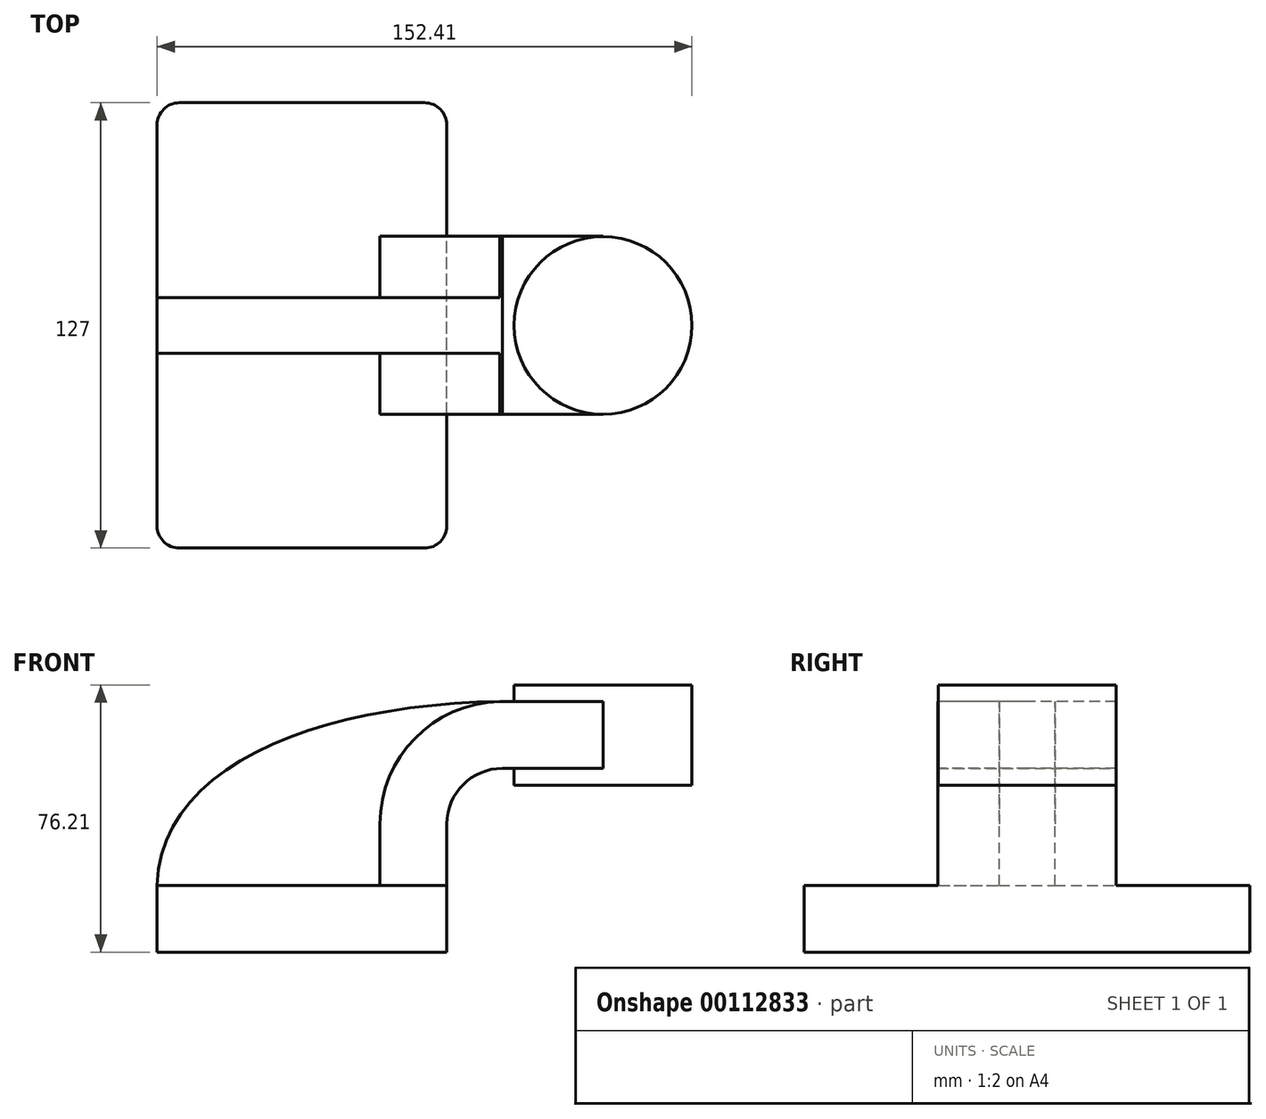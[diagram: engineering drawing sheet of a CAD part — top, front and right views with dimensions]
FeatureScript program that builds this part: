
annotation { "Feature Type Name" : "Feature", "Feature Type Description" : "" }
export const myFeature = defineFeature(function(context is Context, id is Id, definition is map)
    precondition{}
    {
        {
            var Q0;
            Q0=qCreatedBy(makeId("Front.planeOp"),FACE);
            var sketch = newSketch(context, id + "F0", { "sketchPlane" : qUnion([Q0])});
            skLineSegment(sketch, "E0.bottom", {"start": v(41.27, 9.53) * mm, "end": v(-41.28, 9.53) * mm});
            skLineSegment(sketch, "E0.top", {"start": v(41.28, -9.52) * mm, "end": v(-41.27, -9.52) * mm});
            skLineSegment(sketch, "E0.left", {"start": v(41.27, 9.53) * mm, "end": v(41.28, -9.52) * mm});
            skLineSegment(sketch, "E0.right", {"start": v(-41.28, 9.53) * mm, "end": v(-41.27, -9.52) * mm});
            skPoint(sketch, "E0.middle", {"position": v(0, 0) * mm});
            skLineSegment(sketch, "E1.bottom", {"start": v(111.12, 38.1) * mm, "end": v(60.32, 38.1) * mm});
            skLineSegment(sketch, "E1.top", {"start": v(111.12, 66.68) * mm, "end": v(60.32, 66.68) * mm});
            skLineSegment(sketch, "E1.left", {"start": v(111.12, 38.1) * mm, "end": v(111.12, 66.68) * mm});
            skLineSegment(sketch, "E1.right", {"start": v(60.32, 38.1) * mm, "end": v(60.32, 66.68) * mm});
            skPoint(sketch, "E1.middle", {"position": v(85.72, 52.39) * mm});
            skLineSegment(sketch, "E2", {"start": v(41.27, 9.53) * mm, "end": v(41.27, 27) * mm});
            skArc(sketch, "E3", {"start": v(41.27, 27) * mm, "mid": v(45.92, 38.23) * mm, "end": v(57.15, 42.88) * mm});
            skLineSegment(sketch, "E4", {"start": v(57.15, 42.88) * mm, "end": v(85.79, 42.88) * mm});
            skLineSegment(sketch, "E5.0", {"start": v(57.15, 61.93) * mm, "end": v(85.79, 61.93) * mm});
            skArc(sketch, "E5.1", {"start": v(22.22, 27) * mm, "mid": v(32.45, 51.7) * mm, "end": v(57.15, 61.93) * mm});
            skLineSegment(sketch, "E5.2", {"start": v(22.22, 9.53) * mm, "end": v(22.22, 27) * mm});
            skLineSegment(sketch, "E6", {"start": v(85.79, 38.1) * mm, "end": v(85.79, 66.68) * mm});
            skPoint(sketch, "E6.startSnap0", {"position": v(85.72, 38.1) * mm});
            skFitSpline(sketch, "E7", {"points": [v(-41.28, 9.52) * mm, v(57.15, 61.93) * mm], "startDerivative": vector(3.01, 105.74) * mm, "endDerivative": vector(150.34, 1.5) * mm});
            skSolve(sketch);
        }
        {
            var Q0;
            Q0=makeQuery(id+"F0.imprint","IMPRINT",FACE,{"disambiguationData":[TD([[makeQuery(id+"F0.imprint","IMPRINT",EDGE,{"derivedFrom":sQuery(id+"F0.wireOp",EDGE,"E0.top")}),-1.0]])]});
            extrude(context, id + "F1", {"entities" : qUnion([Q0]), "endBound" : BoundingType.SYMMETRIC, "depth" : 127 * mm});
        }
        {
            var Q0;
            {var subQ1=sQuery(id+"F0.wireOp",EDGE,"E2");Q0=makeQuery(id+"F0.imprint","IMPRINT",FACE,{"disambiguationData":[TD([[makeQuery(id+"F0.imprint","IMPRINT",EDGE,{"derivedFrom":subQ1}),1.0]])]});}
            var Q1;
            {var subQ0=sQuery(id+"F0.wireOp",EDGE,"E4");var subQ1=sQuery(id+"F0.wireOp",EDGE,"E1.right");var subQ2=makeQuery(id+"F0.imprint","INTERSECT",VERTEX,{"derivedFrom":[subQ1,subQ0]});Q1=makeQuery(id+"F0.imprint","IMPRINT",FACE,{"disambiguationData":[TD([[makeQuery(id+"F0.imprint","IMPRINT",EDGE,{"disambiguationData":[TD([[subQ2,-1.0]])],"derivedFrom":subQ1}),-1.0]])]});}
            extrude(context, id + "F2", {"entities" : qUnion([Q0, Q1]), "operationType" : NewBodyOperationType.ADD, "endBound" : BoundingType.SYMMETRIC, "depth" : 50.8 * mm});
        }
        {
            var Q0;
            {var subQ3=sQuery(id+"F0.wireOp",EDGE,"E5.2");Q0=makeQuery(id+"F0.imprint","IMPRINT",FACE,{"disambiguationData":[TD([[makeQuery(id+"F0.imprint","IMPRINT",EDGE,{"derivedFrom":subQ3}),1.0]])]});}
            extrude(context, id + "F3", {"entities" : qUnion([Q0]), "operationType" : NewBodyOperationType.ADD, "endBound" : BoundingType.SYMMETRIC, "depth" : 15.88 * mm});
        }
        {
            var Q0;
            {var subQ0=sQuery(id+"F0.wireOp",EDGE,"E1.left");Q0=makeQuery(id+"F0.imprint","IMPRINT",FACE,{"disambiguationData":[TD([[makeQuery(id+"F0.imprint","IMPRINT",EDGE,{"derivedFrom":subQ0}),1.0]])]});}
            var Q1;
            Q1=sQuery(id+"F0.wireOp",EDGE,"E6");
            revolve(context, id + "F4", {"operationType" : NewBodyOperationType.ADD, "entities" : qUnion([Q0]), "axis" : qUnion([Q1]), "revolveType" : RevolveType.FULL});
        }
        {
            var Q0;
            Q0=makeQuery(id+"F1.opExtrude","CAP_EDGE",EDGE,{"disambiguationData":[OSD([sQuery(id+"F0.wireOp",EDGE,"E0.left")])],"isStart":false});
            var Q1;
            Q1=makeQuery(id+"F1.opExtrude","CAP_EDGE",EDGE,{"disambiguationData":[OSD([sQuery(id+"F0.wireOp",EDGE,"E0.right")])],"isStart":false});
            var Q2;
            Q2=makeQuery(id+"F1.opExtrude","CAP_EDGE",EDGE,{"disambiguationData":[OSD([sQuery(id+"F0.wireOp",EDGE,"E0.left")])],"isStart":true});
            var Q3;
            Q3=makeQuery(id+"F1.opExtrude","CAP_EDGE",EDGE,{"disambiguationData":[OSD([sQuery(id+"F0.wireOp",EDGE,"E0.right")])],"isStart":true});
            fillet(context, id + "F5", {"entities" : qUnion([Q0, Q1, Q2, Q3]), "radius" : 6.35 * mm, "tangentPropagation" : true, "allowEdgeOverflow" : false});
        }
    });
